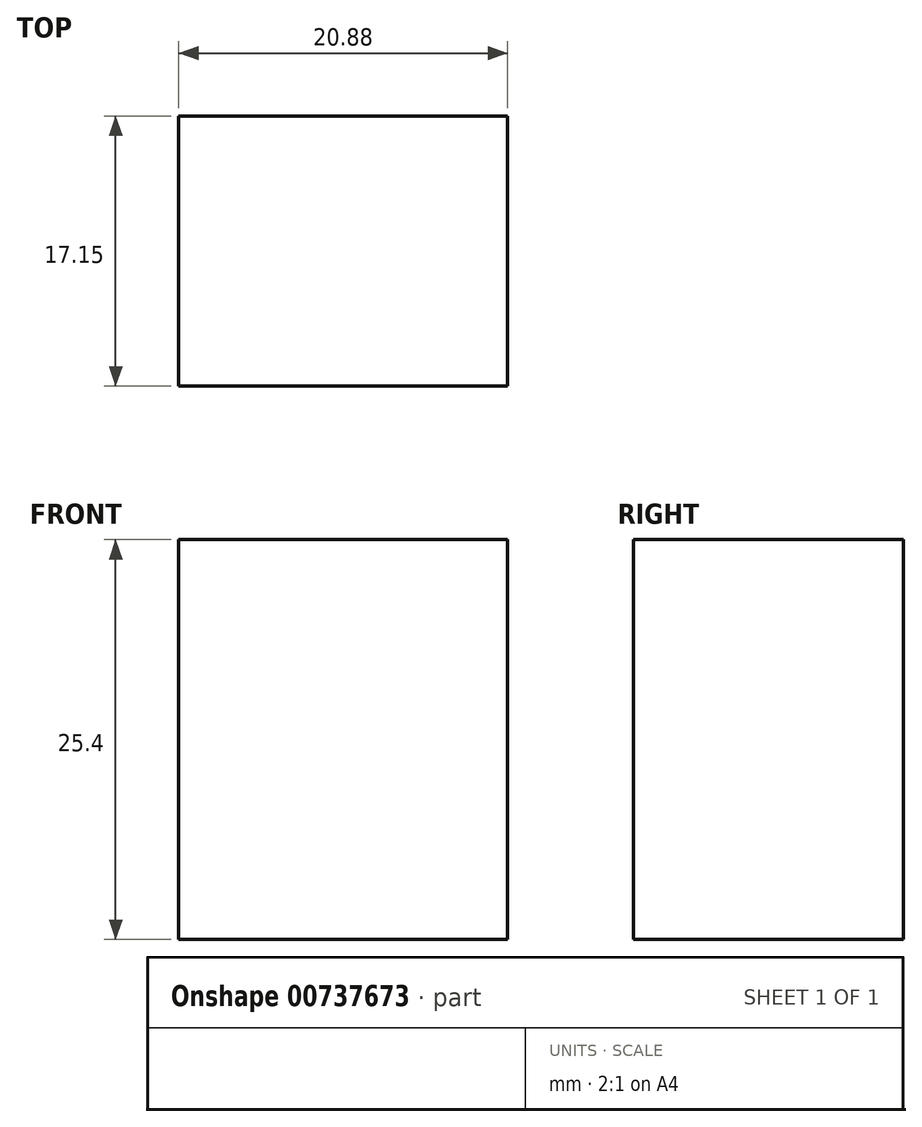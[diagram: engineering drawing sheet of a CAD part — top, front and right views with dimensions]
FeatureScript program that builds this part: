
annotation { "Feature Type Name" : "Feature", "Feature Type Description" : "" }
export const myFeature = defineFeature(function(context is Context, id is Id, definition is map)
    precondition{}
    {
        {
            var Q0;
            Q0=qCreatedBy(makeId("Top.planeOp"),FACE);
            var sketch = newSketch(context, id + "F0", { "sketchPlane" : qUnion([Q0])});
            skLineSegment(sketch, "E0.bottom", {"start": v(-24.03, 16.6) * mm, "end": v(43.26, 16.6) * mm});
            skLineSegment(sketch, "E0.top", {"start": v(-24.03, -12.87) * mm, "end": v(43.26, -12.87) * mm});
            skLineSegment(sketch, "E0.left", {"start": v(-24.03, 16.6) * mm, "end": v(-24.03, -12.87) * mm});
            skLineSegment(sketch, "E0.right", {"start": v(43.26, 16.6) * mm, "end": v(43.26, -12.87) * mm});
            skLineSegment(sketch, "E1.bottom", {"start": v(43.26, -12.87) * mm, "end": v(-24.03, -12.87) * mm});
            skLineSegment(sketch, "E1.top", {"start": v(43.26, 16.6) * mm, "end": v(-24.03, 16.6) * mm});
            skLineSegment(sketch, "E1.left", {"start": v(43.26, -12.87) * mm, "end": v(43.26, 16.6) * mm});
            skLineSegment(sketch, "E1.right", {"start": v(-24.03, -12.87) * mm, "end": v(-24.03, 16.6) * mm});
            skLineSegment(sketch, "E2.bottom", {"start": v(-24.03, 0) * mm, "end": v(-44.91, 0) * mm});
            skLineSegment(sketch, "E2.top", {"start": v(-24.03, 17.15) * mm, "end": v(-44.91, 17.15) * mm});
            skLineSegment(sketch, "E2.left", {"start": v(-24.03, 0) * mm, "end": v(-24.03, 17.15) * mm});
            skLineSegment(sketch, "E2.right", {"start": v(-44.91, 0) * mm, "end": v(-44.91, 17.15) * mm});
            skSolve(sketch);
        }
        {
            var Q0;
            Q0=makeQuery(id+"F0.imprint","IMPRINT",FACE,{"disambiguationData":[TD([[makeQuery(id+"F0.imprint","IMPRINT",EDGE,{"derivedFrom":sQuery(id+"F0.wireOp",EDGE,"E1.bottom")}),-1.0]])]});
            var Q1;
            {var subQ3=sQuery(id+"F0.wireOp",EDGE,"E2.bottom");Q1=makeQuery(id+"F0.imprint","IMPRINT",FACE,{"disambiguationData":[TD([[makeQuery(id+"F0.imprint","IMPRINT",EDGE,{"derivedFrom":subQ3}),-1.0]])]});}
            extrude(context, id + "F1", {"entities" : qUnion([Q0, Q1]), "depth" : 25.4 * mm, "offsetDistance" : 25.4 * mm});
        }
    });
